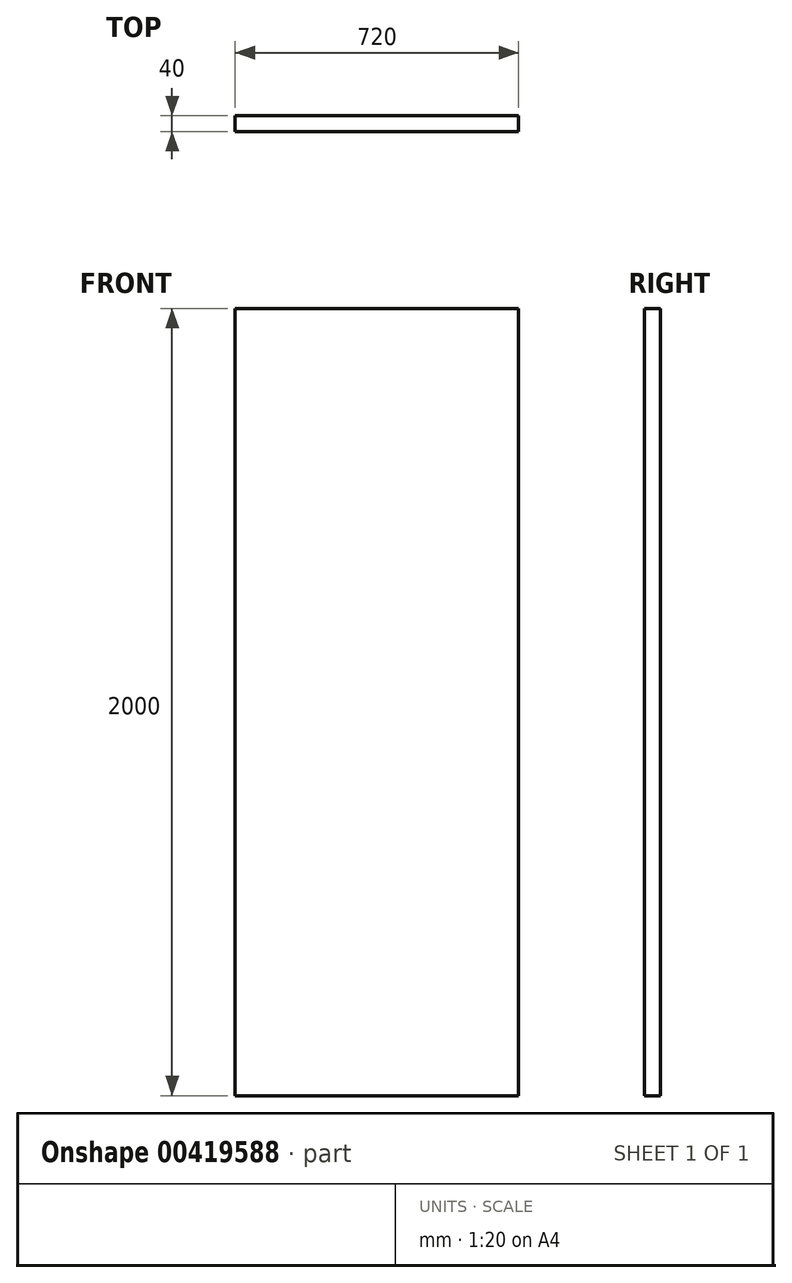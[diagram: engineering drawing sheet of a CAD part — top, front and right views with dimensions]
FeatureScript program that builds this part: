
annotation { "Feature Type Name" : "Feature", "Feature Type Description" : "" }
export const myFeature = defineFeature(function(context is Context, id is Id, definition is map)
    precondition{}
    {
        {
            var Q0;
            Q0=qCreatedBy(makeId("Top.planeOp"),FACE);
            var sketch = newSketch(context, id + "F0", { "sketchPlane" : qUnion([Q0])});
            skLineSegment(sketch, "E0.bottom", {"start": v(-606.8, 18.12) * mm, "end": v(113.2, 18.12) * mm});
            skLineSegment(sketch, "E0.top", {"start": v(-606.8, -21.88) * mm, "end": v(113.2, -21.88) * mm});
            skLineSegment(sketch, "E0.left", {"start": v(-606.8, 18.12) * mm, "end": v(-606.8, -21.88) * mm});
            skLineSegment(sketch, "E0.right", {"start": v(113.2, 18.12) * mm, "end": v(113.2, -21.88) * mm});
            skSolve(sketch);
        }
        {
            var Q0;
            Q0=makeQuery(id+"F0.imprint","IMPRINT",FACE,{"disambiguationData":[TD([[makeQuery(id+"F0.imprint","IMPRINT",EDGE,{"derivedFrom":sQuery(id+"F0.wireOp",EDGE,"E0.bottom")}),-1.0]])]});
            extrude(context, id + "F1", {"entities" : qUnion([Q0]), "depth" : 2000 * mm});
        }
    });
